# Revit family: 306_16728da30a524262845d1bdaf7c404
name_source: partatom
category: Pipe Accessories
units: mm (PartAtom-declared; Revit-internal decimal feet)

## family parameters
Always vertical = Yes
Cut with Voids When Loaded = No
Part Type = Valve - Breaks Into
Round Connector Dimension = Use Diameter
Shared = No
Work Plane-Based = No

## types (2) — shared parameters
Description = 3-way Motorized ball valve MBA132, PN32 external thread with adapters
H1 = 1 mm  [stored 0.00328084 ft]
L2D_Min = 3048 mm
MC = No
Manufacturer = ESBE
QmdConnectorList = 301;D;302;D
URL = http://www.esbe.eu
X15 = 12 mm  [stored 0.0393701 ft]
X15__ve = -12 mm
X16 = 8 mm  [stored 0.0262467 ft]
X16__ve = -8 mm  [stored -0.0262467 ft]
X8 = 6 mm  [stored 0.019685 ft]
Y0 = 5 mm  [stored 0.0164042 ft]
Y11 = 3 mm  [stored 0.00984252 ft]
Z3 = 11 mm
Z4 = 52 mm
Z5 = 3 mm  [stored 0.00984252 ft]
Z5__ve = -3 mm
Z6 = 35 mm
Z6__ve = -35 mm
Z7 = 3 mm  [stored 0.00984252 ft]
magiPartTypeId = 306
magiProductFamilyId = 16728da30a524262845d1bdaf7c404

## per-type parameters (varying)
- MBA132 G1  MMM WA 230VAC 2-P 10NM: CenSd_Y10_6=16 mm; D=25 mm; E=29 mm  [stored 0.0951444 ft]; H=73 mm; L2D=125 mm; W2D=25 mm  [stored 0.082021 ft]; X1=75 mm; X12=44 mm; X12__ve=-44 mm  [stored -0.144357 ft]; X14=4 mm  [stored 0.0131234 ft]; X17=61 mm; X5=3 mm  [stored 0.00984252 ft]; X5__ve=-3 mm; X6=30 mm  [stored 0.0984252 ft]; X7=16 mm; X7__ve=-16 mm; Y1=13 mm  [stored 0.0426509 ft]; Y10=19 mm; Y10__ve=-19 mm; Y12=11 mm; Y13=16 mm; Y14=14 mm  [stored 0.0459318 ft]; Y15=15 mm  [stored 0.0492126 ft]; Y2=13 mm  [stored 0.0426509 ft]; Y4=15 mm  [stored 0.0492126 ft]; Y5=16 mm; Z11=18 mm; Z11__ve=-18 mm; Z2=26 mm  [stored 0.0853018 ft]; Z2__ve=-26 mm; Z8=35 mm; Z9=14 mm  [stored 0.0459318 ft]; Z9__ve=-14 mm  [stored -0.0459318 ft]; magiProductCode=MBA132 G1" MMM WA 230VAC 2-P 10NM; magiProductId=a1dc15ad1ae7495cb6c113459cf9a8
- MBA132 G3/4  MMM WA 230VAC 2-P 10NM: CenSd_Y10_6=13 mm  [stored 0.0426509 ft]; D=20 mm; E=25 mm  [stored 0.082021 ft]; H=65 mm; L2D=110 mm; W2D=20 mm  [stored 0.0656168 ft]; X1=67 mm; X12=37 mm; X12__ve=-37 mm; X14=3 mm  [stored 0.00984252 ft]; X17=54 mm; X5=2 mm  [stored 0.00656168 ft]; X5__ve=-2 mm  [stored -0.00656168 ft]; X6=26 mm  [stored 0.0853018 ft]; X7=14 mm  [stored 0.0459318 ft]; X7__ve=-14 mm  [stored -0.0459318 ft]; Y1=10 mm  [stored 0.0328084 ft]; Y10=15 mm  [stored 0.0492126 ft]; Y10__ve=-15 mm; Y12=9 mm  [stored 0.0295276 ft]; Y13=13 mm  [stored 0.0426509 ft]; Y14=11 mm; Y15=12 mm  [stored 0.0393701 ft]; Y2=10 mm  [stored 0.0328084 ft]; Y4=12 mm  [stored 0.0393701 ft]; Y5=12 mm  [stored 0.0393701 ft]; Z11=17 mm  [stored 0.0557743 ft]; Z11__ve=-17 mm; Z2=23 mm; Z2__ve=-23 mm  [stored -0.0754593 ft]; Z8=33 mm; Z9=13 mm  [stored 0.0426509 ft]; Z9__ve=-13 mm  [stored -0.0426509 ft]; magiProductCode=MBA132 G3/4" MMM WA 230VAC 2-P 10NM; magiProductId=b0016fb93be04706b4c28bc5a8bdce

note: [stored X ft] marks values corroborated as IEEE doubles in the binary element streams (Revit-internal decimal feet)

## geometry (parser evidence)
native form markers: Sweep x3
no freeform markers — native parametric forms only
